# Revit family: IS_Idealrain_BC808_BIM_NL
name_source: partatom
category: Plumbing Fixtures
units: mm (PartAtom-declared; Revit-internal decimal feet)

## family parameters
Always vertical = No
Cut with Voids When Loaded = No
OmniClass Number = 23.45.55.00
OmniClass Title = Sanitary Faucets, Wastes
Part Type = Normal
Room Calculation Point = No
Round Connector Dimension = Use Diameter
Shared = No
Work Plane-Based = No

## types (5) — shared parameters
Accesoires = https://www.idealstandard.nl
Accessories = https://www.idealstandard.nl
Afmetingen = 64 x 60 x 64 mm
AfstandsEenheid = Millimeter
AreaUnits = Millimetres
Artikelomschrijving = IDEALRAIN WALL ELBOW ZYLINDRISCHE 1/2''CONN
Artikelreferentie = IDEALRAIN WALL ELBOW CYLINDRICAL 1/2''CONN
Auteur = Ideal Standard
BIMObjectName = IS_IdealStandard_Showermixers_Idealrain_BC808
BIMobject category = Sanitary
BIMobject category code = Taps & Mixers
BIMobject main category = Sanitary
Beschrijvinggarantie = Herstellergarantie
BimObjectNaam = IS_IdealStandard_Showermixers_Idealrain_BC808
Brand = Ideal Standard
Brand url = http://www.idealstandard.nl
Breedte = 64.39278
ConnectionType = Installation
CurrencyUnit = €
CurrentRevision = 1
Date of publishing = 24/07/2021
Diepte = 60 mm
Douchebak = No
DurationUnit = Years
Edition number = 1
Garantieonderdelen = 5
Garantieunits = Jaren
GemaaktOp = 27/07/2021
HasIntegralShutOffDevice = No
Help = https://www.idealstandard.nl
Hoogte = 64.33341
Hulp = https://www.idealstandard.nl
IFC Classification = Sanitary Terminal
IfcExportAs = IfcValveType
IfcExportType = MIXING
Installatieinstructies = https://www.idealstandard.nl
Installation instructions = https://www.idealstandard.nl
InstallationInstructions = https://www.idealstandard.nl
IsBuiltIn = No
IsHighPressure = No
LinearUnits = Millimetres
MaintenanceInformation = https://www.idealstandard.nl
Manufacturer = Ideal Standard
Manufacturer name = Ideal Standard
ManufacturerURL = https://www.idealstandard.nl
Materiaal = Messing
Material = Brass
Material main = Brass
Merk = Ideal Standard
ModelReference = IDEALRAIN WALL ELBOW CYLINDRICAL 1/2''CONN
Montageinstuctie = https://www.idealstandard.nl
NBS Reference Code = 45-35-70/335
NBS Reference Description = Shower mixers
Name = Showermixers_Idealrain_BC808_IdealStandard
NettWeight = 0.31
Nettogewicht = 0.31
NominalDepth = 60 mm
NominalHeight = 64 mm
NominalLength = 60 mm
NominalWidth = 64 mm
Normen = Showermixers_Idealrain_BC808_IdealStandard
OppervlakteEenheid = Millimeter
Product Guid = 2a70d760-05e5-406b-a3a4-a9b7e8e999b2
Product SKU = BC808
Product certification = https://www.idealstandard.nl
Product data url = https://bimobject.com
Product family = Sanitary
Product group = Showers
Product name = IDEALRAIN WALL ELBOW CYLINDRICAL 1/2''CONN
Product url = https://www.idealstandard.nl
ProductInformation = https://www.idealstandard.nl
ProductSoort = Sanitary
Productinformatie = https://www.idealstandard.nl
QR code = http://bimobject.com
Referentie = IDEALRAIN WALL ELBOW CYLINDRICAL 1/2''CONN
Revisie = 1
Shape = Cylindrical
Size = 64 x 60 x 64 mm
Space = Internal
SpareParts = https://www.idealstandard.nl
Technical description = https://www.idealstandard.nl
Telefoonnummer = 077 355 08 08
TestPressure = 10 Bar
Testdruk = 10 Bar
Typeconnectie = Installation
URL = https://www.idealstandard.nl
Uniclass 2015 Code = Pr_40_20_87_80
Uniclass 2015 Name = Shower thermostatic valves
Uniclass2015Beschrijving = Shower thermostatic valves
Uniclass2015Code = Pr_40_20_87_80
Uniclass2015Referentie = Pr_40_20_87_80
Uniclass2015Title = Shower thermostatic valves
Uniclass2015Version = v1.22
Urlproducent = https://www.idealstandard.nl
ValutaEenheid = Euro
Versie = 1
Version = 1
VolumeUnits = Litres
Volumeunits = Liters
Vorm = zylindrisch
WRASURL = https://www.wrasapprovals.co.uk
WarrantyDescription = Manufacturer warranty
WarrantyDurationUnit = Years
Wisselstukken = https://www.idealstandard.nl
Youtube clip = https://www.youtube.com
zero-valued in all types: BrutoGewicht, Cost, Lengte, Vervangingskosten

## per-type parameters (varying)
| type | Afwerking | Artikelnummer | BarCode | Barcode | Color | Description | Eigenschappen | Features | Finish | GTIN code | Kleur | MainColor | Model | ModelNumber |
| BC808AA - IDEALRAIN WALL ELBOW CYLINDRICAL 1/2''CONN - CHROME | Chrom | BC808AA | 3800861086345 | 3800861086345 | Chrom | IDEALRAIN WALL ELBOW ZYLINDRISCHE 1/2''CONN - CHROM | WALL ELBOW ZYLINDRISCHE 1/2''CONN - CHROM | WALL ELBOW ZYLINDRISCHE 1/2''CONN - CHROM | Chrom | https://3800861086345 | Chrom | Chrom | BC808AA | BC808AA |
| BC808A5 - IDEALRAIN WALL ELBOW CYLINDRICAL 1/2''CONN - MAGNETIC GREY | magnetisch grau | BC808A5 | 3800861087540 | 3800861087540 | magnetisch grau | IDEALRAIN WALL ELBOW ZYLINDRISCHE 1/2''CONN - MAGNETISCHES GRAU | WALL ELBOW ZYLINDRISCHE 1/2''CONN - MAGNETISCHES GRAU | WALL ELBOW ZYLINDRISCHE 1/2''CONN - MAGNETISCHES GRAU | magnetisch grau | https://3800861087540 | magnetisch grau | magnetisch grau | BC808A5 | BC808A5 |
| BC808XG - IDEALRAIN WALL ELBOW CYLINDRICAL 1/2''CONN - SILK BLACK | Seide schwarz | BC808XG | 3800861101192 | 3800861101192 | Seide schwarz | IDEALRAIN WALL ELBOW ZYLINDRISCHE 1/2''CONN - SEIDE SCHWARZ | WALL ELBOW ZYLINDRISCHE 1/2''CONN - SEIDE SCHWARZ | WALL ELBOW ZYLINDRISCHE 1/2''CONN - SEIDE SCHWARZ | Seide schwarz | https://3800861101192 | Seide schwarz | Seide schwarz | BC808XG | BC808XG |
| BC808GN - IDEALRAIN WALL ELBOW CYLINDRICAL 1/2''CONN - SILVER STORM | silberner Sturm | BC808GN | 3800861086741 | 3800861086741 | silberner Sturm | IDEALRAIN WALL ELBOW ZYLINDRISCHE 1/2''CONN - SILBER STURM | WALL ELBOW ZYLINDRISCHE 1/2''CONN - SILBER STURM | WALL ELBOW ZYLINDRISCHE 1/2''CONN - SILBER STURM | silberner Sturm | https://3800861086741 | silberner Sturm | silberner Sturm | BC808GN | BC808GN |
| BC808A2 - IDEALRAIN WALL ELBOW CYLINDRICAL 1/2''CONN - BRUSH GOLD | Pinsel gold | BC808A2 | 3800861087144 | 3800861087144 | Pinsel gold | IDEALRAIN WALL ELBOW ZYLINDRISCHE 1/2''CONN - PINSEL GOLD | WALL ELBOW ZYLINDRISCHE 1/2''CONN - PINSEL GOLD | WALL ELBOW ZYLINDRISCHE 1/2''CONN - PINSEL GOLD | Pinsel gold | https://3800861087144 | Pinsel gold | Pinsel gold | BC808A2 | BC808A2 |

## geometry (parser evidence)
native form markers: Sweep x3
no freeform markers — native parametric forms only
